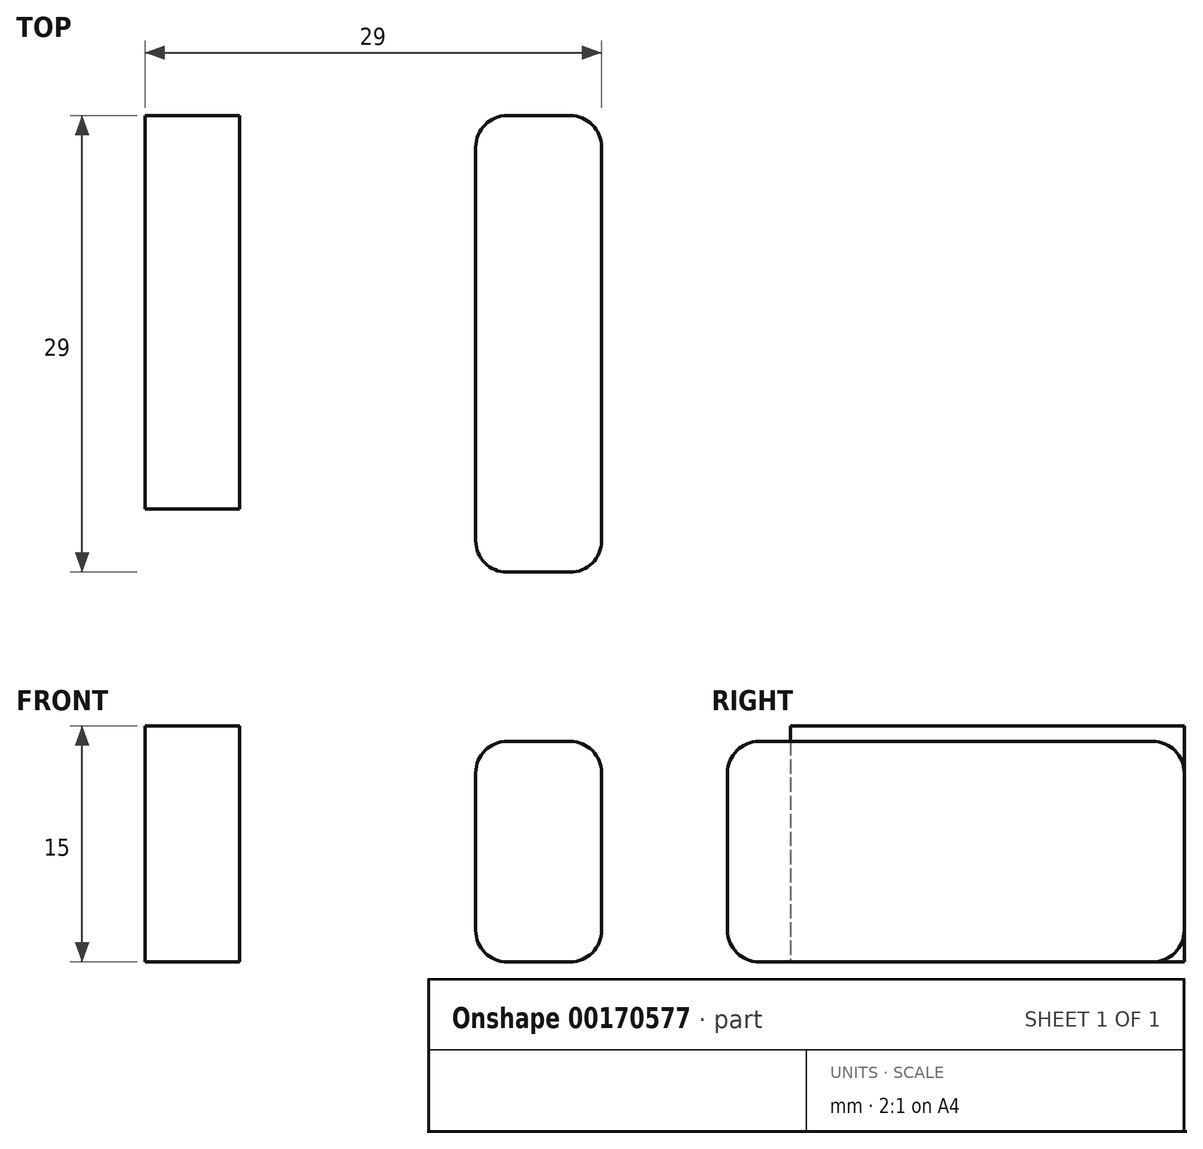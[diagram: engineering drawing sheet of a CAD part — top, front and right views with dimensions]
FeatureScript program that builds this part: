
annotation { "Feature Type Name" : "Feature", "Feature Type Description" : "" }
export const myFeature = defineFeature(function(context is Context, id is Id, definition is map)
    precondition{}
    {
        {
            var Q0;
            Q0=qCreatedBy(makeId("Top.planeOp"),FACE);
            var sketch = newSketch(context, id + "F0", { "sketchPlane" : qUnion([Q0])});
            skLineSegment(sketch, "E0.bottom", {"start": v(-6, 0) * mm, "end": v(0, 0) * mm});
            skLineSegment(sketch, "E0.top", {"start": v(-6, -25) * mm, "end": v(0, -25) * mm});
            skLineSegment(sketch, "E0.left", {"start": v(-6, 0) * mm, "end": v(-6, -25) * mm});
            skLineSegment(sketch, "E0.right", {"start": v(0, 0) * mm, "end": v(0, -25) * mm});
            skSolve(sketch);
        }
        {
            var Q0;
            Q0 = qSketchRegion(id + "F0", true);
            extrude(context, id + "F1", {"entities" : qUnion([Q0]), "depth" : 15 * mm});
        }
        {
            var Q0;
            Q0=qCreatedBy(makeId("Top.planeOp"),FACE);
            var sketch = newSketch(context, id + "F2", { "sketchPlane" : qUnion([Q0])});
            skLineSegment(sketch, "E1.bottom", {"start": v(15, 0) * mm, "end": v(23, 0) * mm});
            skLineSegment(sketch, "E1.top", {"start": v(15, -29) * mm, "end": v(23, -29) * mm});
            skLineSegment(sketch, "E1.left", {"start": v(15, 0) * mm, "end": v(15, -29) * mm});
            skLineSegment(sketch, "E1.right", {"start": v(23, 0) * mm, "end": v(23, -29) * mm});
            skSolve(sketch);
        }
        {
            var Q0;
            Q0 = qSketchRegion(id + "F2", true);
            extrude(context, id + "F3", {"entities" : qUnion([Q0]), "depth" : 14 * mm});
        }
        {
            var Q0;
            Q0=makeQuery(id+"F3.opExtrude","SWEPT_EDGE",EDGE,{"disambiguationData":[OSD([sQuery(id+"F2.wireOp",EDGE,"E1.top"),sQuery(id+"F2.wireOp",EDGE,"E1.right")])]});
            var Q1;
            Q1=makeQuery(id+"F3.opExtrude","SWEPT_EDGE",EDGE,{"disambiguationData":[OSD([sQuery(id+"F2.wireOp",EDGE,"E1.top"),sQuery(id+"F2.wireOp",EDGE,"E1.left")])]});
            var Q2;
            Q2=makeQuery(id+"F3.opExtrude","SWEPT_EDGE",EDGE,{"disambiguationData":[OSD([sQuery(id+"F2.wireOp",EDGE,"E1.bottom"),sQuery(id+"F2.wireOp",EDGE,"E1.right")])]});
            var Q3;
            Q3=makeQuery(id+"F3.opExtrude","SWEPT_EDGE",EDGE,{"disambiguationData":[OSD([sQuery(id+"F2.wireOp",EDGE,"E1.bottom"),sQuery(id+"F2.wireOp",EDGE,"E1.left")])]});
            var Q4;
            Q4=makeQuery(id+"F3.opExtrude","CAP_EDGE",EDGE,{"disambiguationData":[OSD([sQuery(id+"F2.wireOp",EDGE,"E1.top")])],"isStart":false});
            var Q5;
            Q5=makeQuery(id+"F3.opExtrude","CAP_EDGE",EDGE,{"disambiguationData":[OSD([sQuery(id+"F2.wireOp",EDGE,"E1.right")])],"isStart":false});
            var Q6;
            Q6=makeQuery(id+"F3.opExtrude","CAP_EDGE",EDGE,{"disambiguationData":[OSD([sQuery(id+"F2.wireOp",EDGE,"E1.left")])],"isStart":false});
            var Q7;
            Q7=makeQuery(id+"F3.opExtrude","CAP_EDGE",EDGE,{"disambiguationData":[OSD([sQuery(id+"F2.wireOp",EDGE,"E1.bottom")])],"isStart":false});
            var Q8;
            Q8=makeQuery(id+"F3.opExtrude","CAP_EDGE",EDGE,{"disambiguationData":[OSD([sQuery(id+"F2.wireOp",EDGE,"E1.left")])],"isStart":true});
            var Q9;
            Q9=makeQuery(id+"F3.opExtrude","CAP_EDGE",EDGE,{"disambiguationData":[OSD([sQuery(id+"F2.wireOp",EDGE,"E1.right")])],"isStart":true});
            var Q10;
            Q10=makeQuery(id+"F3.opExtrude","CAP_EDGE",EDGE,{"disambiguationData":[OSD([sQuery(id+"F2.wireOp",EDGE,"E1.top")])],"isStart":true});
            var Q11;
            Q11=makeQuery(id+"F3.opExtrude","CAP_EDGE",EDGE,{"disambiguationData":[OSD([sQuery(id+"F2.wireOp",EDGE,"E1.bottom")])],"isStart":true});
            fillet(context, id + "F4", {"entities" : qUnion([Q0, Q1, Q2, Q3, Q4, Q5, Q6, Q7, Q8, Q9, Q10, Q11]), "radius" : 2 * mm, "tangentPropagation" : true, "allowEdgeOverflow" : false});
        }
    });
